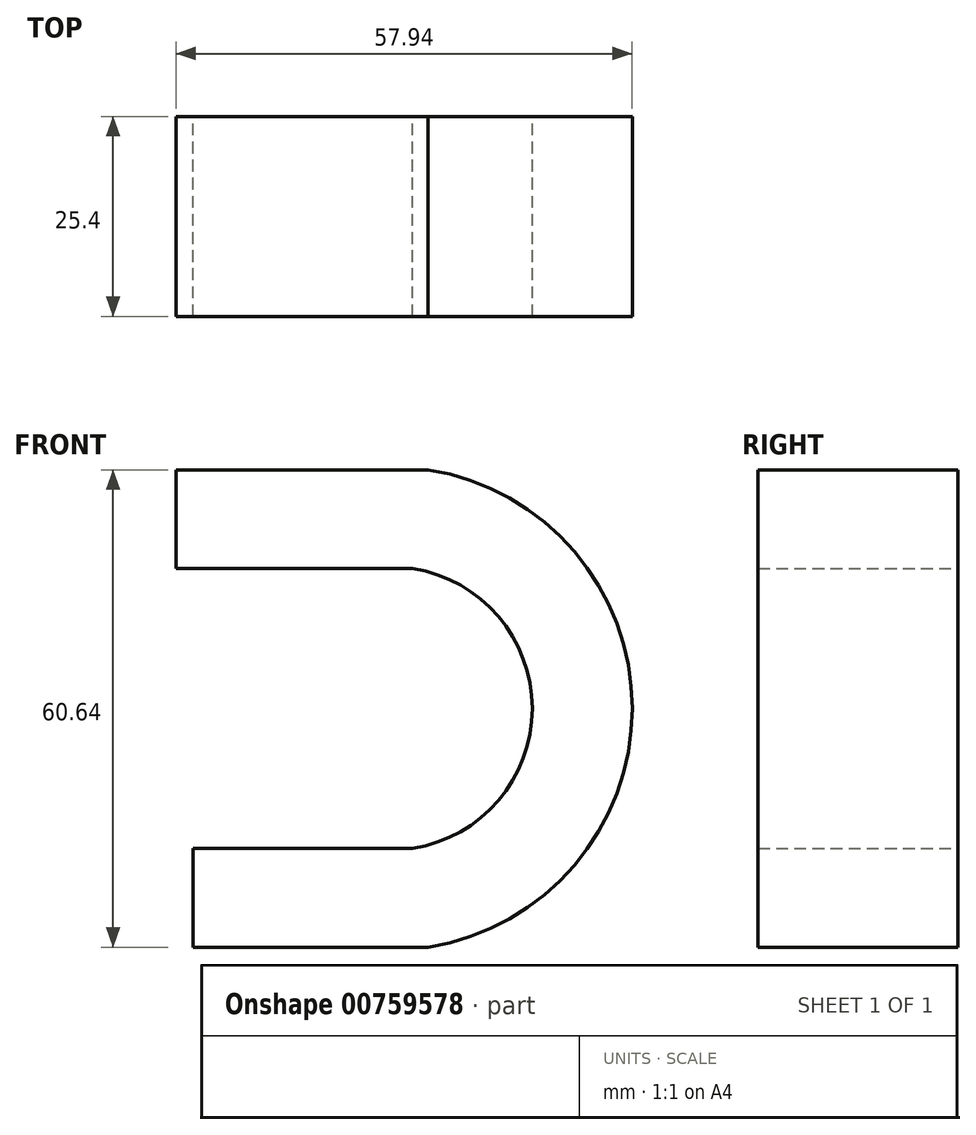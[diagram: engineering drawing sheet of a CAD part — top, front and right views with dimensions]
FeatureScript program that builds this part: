
annotation { "Feature Type Name" : "Feature", "Feature Type Description" : "" }
export const myFeature = defineFeature(function(context is Context, id is Id, definition is map)
    precondition{}
    {
        {
            var Q0;
            Q0=qCreatedBy(makeId("Front.planeOp"),FACE);
            var sketch = newSketch(context, id + "F0", { "sketchPlane" : qUnion([Q0])});
            skArc(sketch, "E0", {"start": v(0, -35.56) * mm, "mid": v(15.2, -17.78) * mm, "end": v(0, 0) * mm});
            skLineSegment(sketch, "E1", {"start": v(0, 0) * mm, "end": v(-30.05, 0) * mm});
            skLineSegment(sketch, "E2", {"start": v(0, -35.56) * mm, "end": v(-27.86, -35.56) * mm});
            skArc(sketch, "E3.0", {"start": v(1.98, -48.1) * mm, "mid": v(27.9, -17.78) * mm, "end": v(1.98, 12.54) * mm});
            skLineSegment(sketch, "E4", {"start": v(1.98, 12.54) * mm, "end": v(-30.05, 12.54) * mm});
            skLineSegment(sketch, "E5", {"start": v(1.98, -48.1) * mm, "end": v(-27.86, -48.1) * mm});
            skLineSegment(sketch, "E6", {"start": v(-27.86, -48.1) * mm, "end": v(-27.86, -35.56) * mm});
            skLineSegment(sketch, "E7", {"start": v(-30.05, 0) * mm, "end": v(-30.05, 12.54) * mm});
            skSolve(sketch);
        }
        {
            var Q0;
            Q0=makeQuery(id+"F0.imprint","IMPRINT",FACE,{"disambiguationData":[TD([[makeQuery(id+"F0.imprint","IMPRINT",EDGE,{"derivedFrom":sQuery(id+"F0.wireOp",EDGE,"E0")}),-1.0]])]});
            extrude(context, id + "F1", {"entities" : qUnion([Q0]), "depth" : 25.4 * mm, "offsetDistance" : 25.4 * mm});
        }
    });
